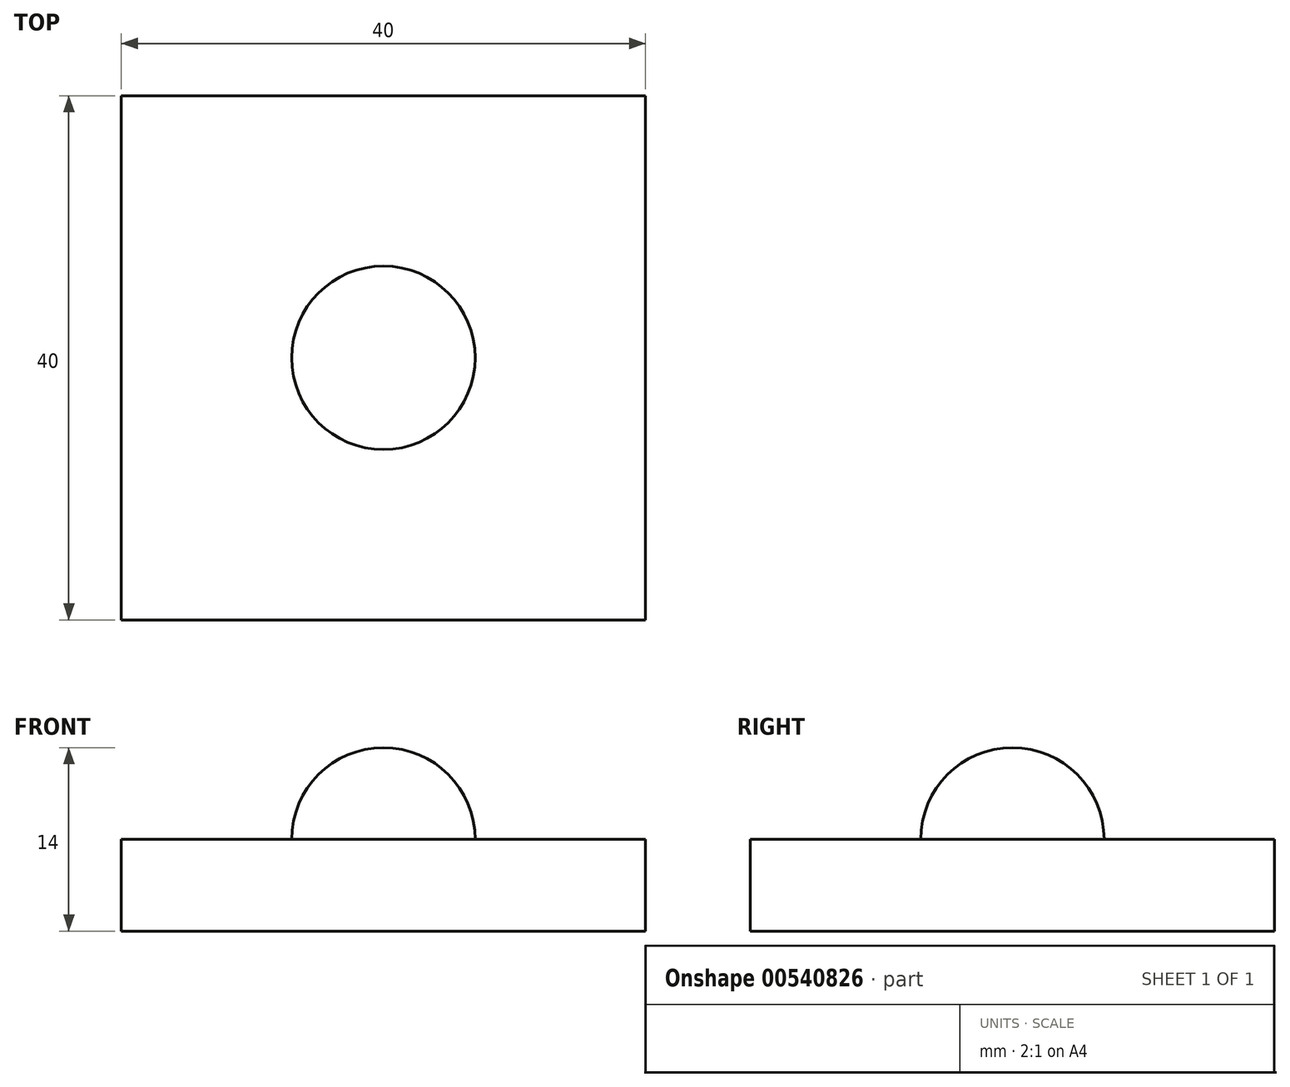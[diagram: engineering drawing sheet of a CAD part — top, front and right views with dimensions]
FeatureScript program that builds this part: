
annotation { "Feature Type Name" : "Feature", "Feature Type Description" : "" }
export const myFeature = defineFeature(function(context is Context, id is Id, definition is map)
    precondition{}
    {
        {
            var Q0;
            Q0=qCreatedBy(makeId("Top.planeOp"),FACE);
            var sketch = newSketch(context, id + "F0", { "sketchPlane" : qUnion([Q0])});
            skLineSegment(sketch, "E0.bottom", {"start": v(20, -20) * mm, "end": v(-20, -20) * mm});
            skLineSegment(sketch, "E0.top", {"start": v(20, 20) * mm, "end": v(-20, 20) * mm});
            skLineSegment(sketch, "E0.left", {"start": v(20, -20) * mm, "end": v(20, 20) * mm});
            skLineSegment(sketch, "E0.right", {"start": v(-20, -20) * mm, "end": v(-20, 20) * mm});
            skPoint(sketch, "E0.middle", {"position": v(0, 0) * mm});
            skSolve(sketch);
        }
        {
            var Q0;
            Q0=makeQuery(id+"F0.imprint","IMPRINT",FACE,{"disambiguationData":[TD([[makeQuery(id+"F0.imprint","IMPRINT",EDGE,{"derivedFrom":sQuery(id+"F0.wireOp",EDGE,"E0.bottom")}),-1.0]])]});
            extrude(context, id + "F1", {"entities" : qUnion([Q0]), "depth" : 7 * mm, "offsetDistance" : 25 * mm});
        }
        {
            var Q0;
            Q0=makeQuery(id+"F1.opExtrude","CAP_FACE",FACE,{"disambiguationData":[OSD([sQuery(id+"F0.wireOp",EDGE,"E0.bottom"),sQuery(id+"F0.wireOp",EDGE,"E0.top"),sQuery(id+"F0.wireOp",EDGE,"E0.left"),sQuery(id+"F0.wireOp",EDGE,"E0.right")])],"isStart":false});
            var sketch = newSketch(context, id + "F2", { "sketchPlane" : qUnion([Q0])});
            skArc(sketch, "E1", {"start": v(-7, 0) * mm, "mid": v(0, -7) * mm, "end": v(7, 0) * mm});
            skPoint(sketch, "E2", {"position": v(7, 0) * mm});
            skPoint(sketch, "E3", {"position": v(-7, 0) * mm});
            skLineSegment(sketch, "E4", {"start": v(7, 0) * mm, "end": v(-7, 0) * mm});
            skSolve(sketch);
        }
        {
            var Q0;
            Q0=makeQuery(id+"F2.imprint","IMPRINT",FACE,{"disambiguationData":[TD([[makeQuery(id+"F2.imprint","IMPRINT",EDGE,{"derivedFrom":sQuery(id+"F2.wireOp",EDGE,"E1")}),1.0]])]});
            var Q1;
            Q1=sQuery(id+"F2.wireOp",EDGE,"E4");
            revolve(context, id + "F3", {"operationType" : NewBodyOperationType.ADD, "entities" : qUnion([Q0]), "axis" : qUnion([Q1]), "revolveType" : RevolveType.FULL});
        }
    });
